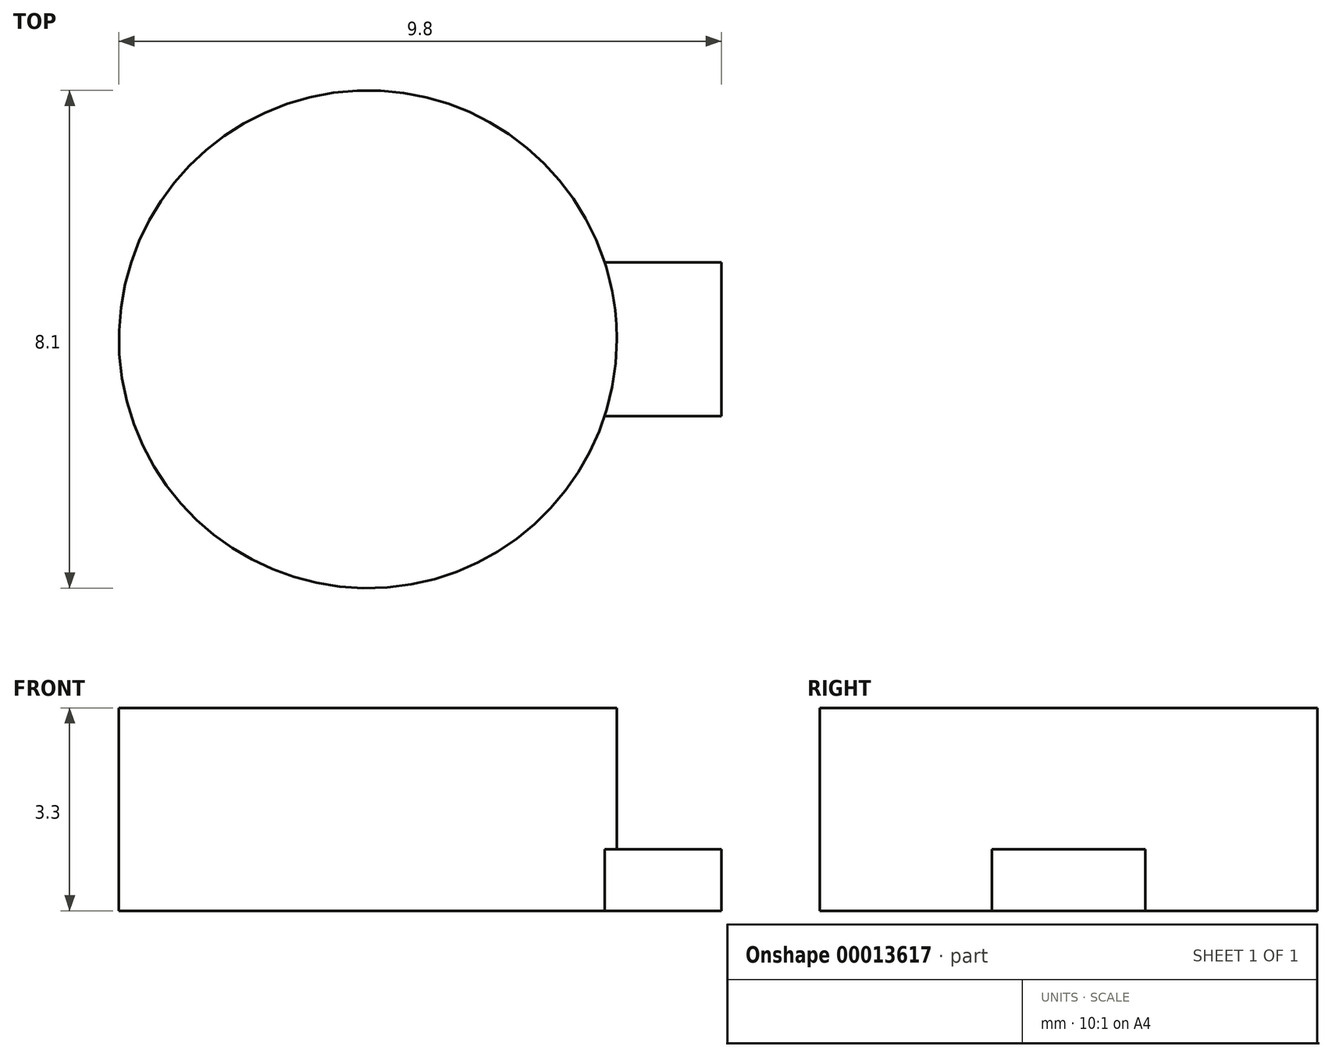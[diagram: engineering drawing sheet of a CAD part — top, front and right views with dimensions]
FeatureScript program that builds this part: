
annotation { "Feature Type Name" : "Feature", "Feature Type Description" : "" }
export const myFeature = defineFeature(function(context is Context, id is Id, definition is map)
    precondition{}
    {
        {
            var Q0;
            Q0=qCreatedBy(makeId("Top.planeOp"),FACE);
            var sketch = newSketch(context, id + "F0", { "sketchPlane" : qUnion([Q0])});
            skCircle(sketch, "E0", {"center": v(0, 0) * mm, "radius": 4.05 * mm});
            skLineSegment(sketch, "E1.bottom", {"start": v(1.67, 1.25) * mm, "end": v(5.75, 1.25) * mm});
            skLineSegment(sketch, "E1.top", {"start": v(1.67, -1.25) * mm, "end": v(5.75, -1.25) * mm});
            skLineSegment(sketch, "E1.left", {"start": v(1.67, 1.25) * mm, "end": v(1.67, -1.25) * mm});
            skLineSegment(sketch, "E1.right", {"start": v(5.75, 1.25) * mm, "end": v(5.75, -1.25) * mm});
            skSolve(sketch);
        }
        {
            var Q0;
            {var subQ0=sQuery(id+"F0.wireOp",EDGE,"E1.left");Q0=makeQuery(id+"F0.imprint","IMPRINT",FACE,{"disambiguationData":[TD([[makeQuery(id+"F0.imprint","IMPRINT",EDGE,{"derivedFrom":subQ0}),-1.0]])]});}
            var Q1;
            {var subQ0=sQuery(id+"F0.wireOp",EDGE,"E1.left");Q1=makeQuery(id+"F0.imprint","IMPRINT",FACE,{"disambiguationData":[TD([[makeQuery(id+"F0.imprint","IMPRINT",EDGE,{"derivedFrom":subQ0}),1.0]])]});}
            extrude(context, id + "F1", {"entities" : qUnion([Q0, Q1]), "depth" : 3.3 * mm});
        }
        {
            var Q0;
            {var subQ0=sQuery(id+"F0.wireOp",EDGE,"E1.right");Q0=makeQuery(id+"F0.imprint","IMPRINT",FACE,{"disambiguationData":[TD([[makeQuery(id+"F0.imprint","IMPRINT",EDGE,{"derivedFrom":subQ0}),-1.0]])]});}
            extrude(context, id + "F2", {"entities" : qUnion([Q0]), "operationType" : NewBodyOperationType.ADD, "depth" : 1 * mm});
        }
    });
